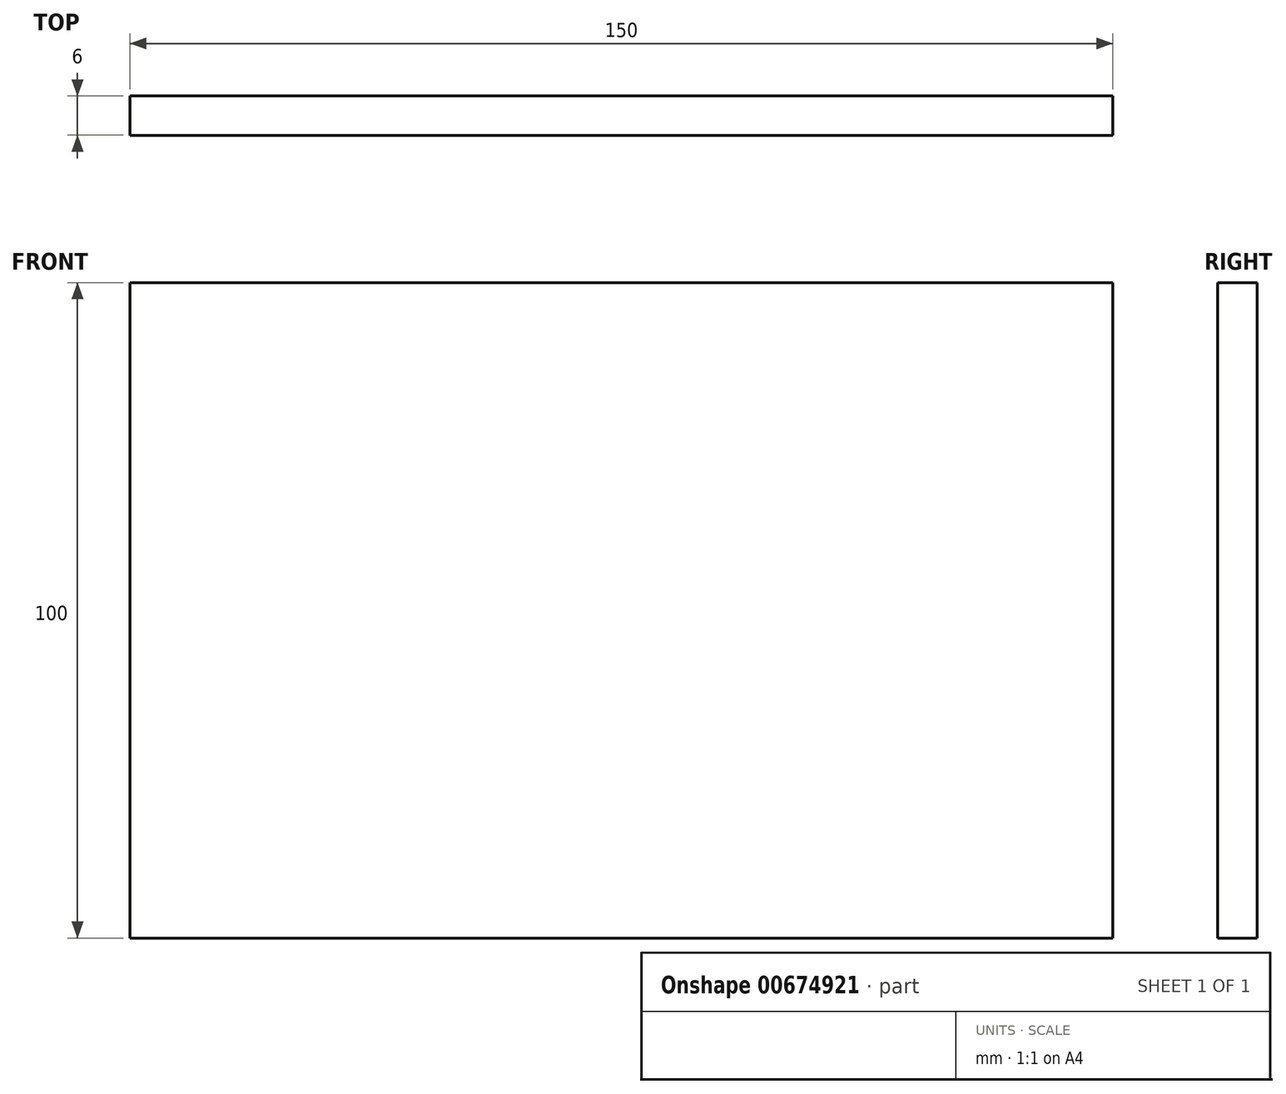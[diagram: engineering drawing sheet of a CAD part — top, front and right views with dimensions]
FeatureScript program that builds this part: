
annotation { "Feature Type Name" : "Feature", "Feature Type Description" : "" }
export const myFeature = defineFeature(function(context is Context, id is Id, definition is map)
    precondition{}
    {
        {
            var Q0;
            Q0=qCreatedBy(makeId("Top.planeOp"),FACE);
            var sketch = newSketch(context, id + "F0", { "sketchPlane" : qUnion([Q0])});
            skLineSegment(sketch, "E0.bottom", {"start": v(-19.93, -3.8) * mm, "end": v(130.07, -3.8) * mm});
            skLineSegment(sketch, "E0.top", {"start": v(-19.93, 2.2) * mm, "end": v(130.07, 2.2) * mm});
            skLineSegment(sketch, "E0.left", {"start": v(-19.93, -3.8) * mm, "end": v(-19.93, 2.2) * mm});
            skLineSegment(sketch, "E0.right", {"start": v(130.07, -3.8) * mm, "end": v(130.07, 2.2) * mm});
            skSolve(sketch);
        }
        {
            var Q0;
            Q0=makeQuery(id+"F0.imprint","IMPRINT",FACE,{"disambiguationData":[TD([[makeQuery(id+"F0.imprint","IMPRINT",EDGE,{"derivedFrom":sQuery(id+"F0.wireOp",EDGE,"E0.bottom")}),1.0]])]});
            extrude(context, id + "F1", {"entities" : qUnion([Q0]), "depth" : 100 * mm, "offsetDistance" : 25 * mm});
        }
    });
